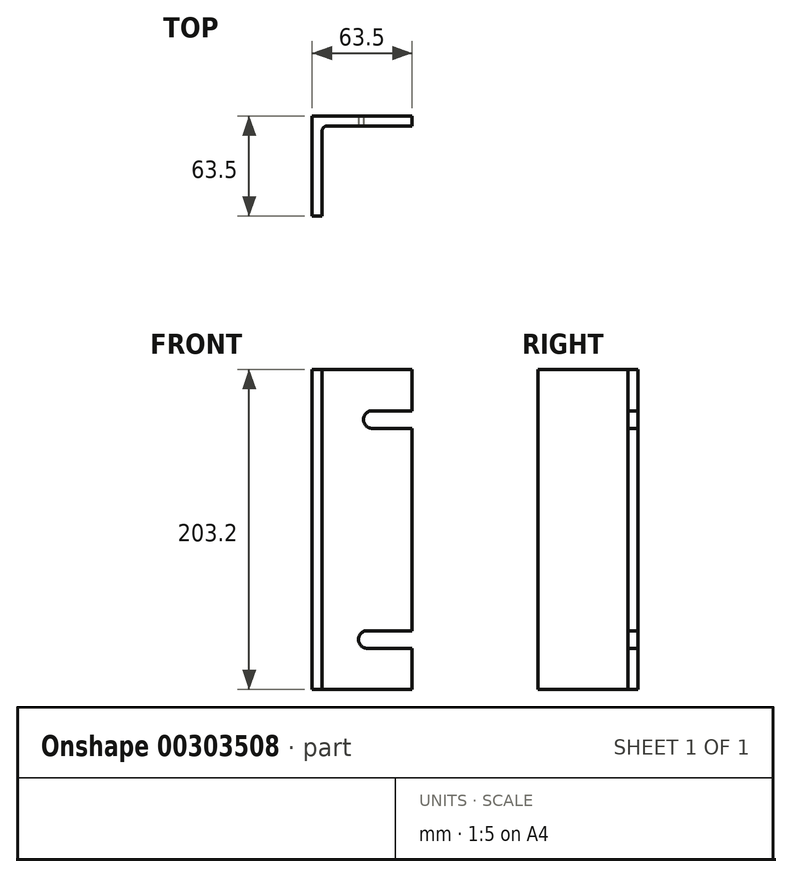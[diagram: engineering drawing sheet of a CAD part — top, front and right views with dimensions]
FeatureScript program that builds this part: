
annotation { "Feature Type Name" : "Feature", "Feature Type Description" : "" }
export const myFeature = defineFeature(function(context is Context, id is Id, definition is map)
    precondition{}
    {
        {
            var Q0;
            Q0=qCreatedBy(makeId("Top.planeOp"),FACE);
            var sketch = newSketch(context, id + "F0", { "sketchPlane" : qUnion([Q0])});
            skLineSegment(sketch, "E0.bottom", {"start": v(0, -63.5) * mm, "end": v(6.35, -63.5) * mm});
            skLineSegment(sketch, "E0.top", {"start": v(0, 0) * mm, "end": v(6.35, 0) * mm});
            skLineSegment(sketch, "E0.left", {"start": v(0, -63.5) * mm, "end": v(0, 0) * mm});
            skLineSegment(sketch, "E0.right", {"start": v(6.35, -63.5) * mm, "end": v(6.35, -9.53) * mm});
            skLineSegment(sketch, "E1.bottom", {"start": v(0, 0) * mm, "end": v(63.5, 0) * mm});
            skLineSegment(sketch, "E1.top", {"start": v(9.52, -6.35) * mm, "end": v(63.5, -6.35) * mm});
            skLineSegment(sketch, "E1.left", {"start": v(0, 0) * mm, "end": v(0, -6.35) * mm});
            skLineSegment(sketch, "E1.right", {"start": v(63.5, 0) * mm, "end": v(63.5, -6.35) * mm});
            skPoint(sketch, "E2.visualSharp", {"position": v(6.35, -6.35) * mm});
            skArc(sketch, "E2.filletArc", {"start": v(9.52, -6.35) * mm, "mid": v(7.28, -7.28) * mm, "end": v(6.35, -9.53) * mm});
            skSolve(sketch);
        }
        {
            var Q0;
            Q0 = qSketchRegion(id + "F0", true);
            extrude(context, id + "F1", {"entities" : qUnion([Q0]), "depth" : 203.2 * mm});
        }
        {
            var Q0;
            Q0=makeQuery(id+"F1.opExtrude","SWEPT_FACE",FACE,{"disambiguationData":[OSD([sQuery(id+"F0.wireOp",EDGE,"E1.top")])]});
            var sketch = newSketch(context, id + "F2", { "sketchPlane" : qUnion([Q0])});
            skLineSegment(sketch, "E3", {"start": v(34.9, 37.3) * mm, "end": v(63.5, 37.3) * mm});
            skLineSegment(sketch, "E4", {"start": v(34.92, 26.18) * mm, "end": v(63.5, 26.18) * mm});
            skLineSegment(sketch, "E5", {"start": v(38.1, 177) * mm, "end": v(63.5, 177) * mm});
            skLineSegment(sketch, "E6", {"start": v(38.1, 165.88) * mm, "end": v(63.5, 165.88) * mm});
            skArc(sketch, "E7", {"start": v(38.1, 177) * mm, "mid": v(32.54, 171.44) * mm, "end": v(38.1, 165.88) * mm});
            skArc(sketch, "E8", {"start": v(34.92, 37.3) * mm, "mid": v(29.37, 31.74) * mm, "end": v(34.92, 26.18) * mm});
            skSolve(sketch);
        }
        {
            var Q0;
            {var subQ0=sQuery(id+"F2.wireOp",EDGE,"E5");Q0=makeQuery(id+"F2.imprint","IMPRINT",FACE,{"disambiguationData":[TD([[makeQuery(id+"F2.imprint","IMPRINT",EDGE,{"derivedFrom":subQ0}),-1.0]])]});}
            var Q1;
            {var subQ3=sQuery(id+"F2.wireOp",EDGE,"E4");Q1=makeQuery(id+"F2.imprint","IMPRINT",FACE,{"disambiguationData":[TD([[makeQuery(id+"F2.imprint","IMPRINT",EDGE,{"derivedFrom":subQ3}),1.0]])]});}
            extrude(context, id + "F3", {"entities" : qUnion([Q0, Q1]), "operationType" : NewBodyOperationType.REMOVE, "oppositeDirection" : true, "depth" : 25.4 * mm});
        }
    });
